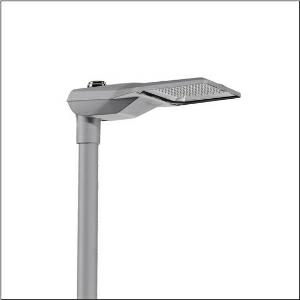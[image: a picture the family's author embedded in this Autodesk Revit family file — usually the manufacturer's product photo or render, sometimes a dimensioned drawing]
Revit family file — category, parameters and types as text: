
# Revit family: streetlight_sl_21_midi___p0_8a_5xe7u27n08lb_052f
name_source: partatom
category: Lighting Fixtures
units: mm (PartAtom-declared; Revit-internal decimal feet)

## family parameters
Cut with Voids When Loaded = No
Host = Face
Light Source = No
Part Type = Normal
Room Calculation Point = No
Round Connector Dimension = Use Diameter
Shared = No

## types (1)
- --- (1 x LED, 11980 lm, 98.3 W, 2200K)
    Apparent Load = 98 VA
    CIE Flux Codes = 33 69 96 100 100
    Color Rendering = 70
    Color Temperature = 2200K
    Default Elevation = 1800 mm
    Description = Streetlight SL 21 midi, mast luminaire, primary light control with lens, of PMMA, primary optical cover: cover, of toughened safety glass, transparent, light distribution: P0.8a, light emission: direct distribution, primary light characteristic: asymmetric, installation type: side-entry, LED, 3G 2.5mm², High Power LED, rated luminous flux: 11.980lm, luminous efficacy: 122lm/W, light colour: 722, colour temperature: 2200K, control gear: NEMA (7pin), control: flexible luminous flux parameterisation, time-dependent luminous flux control, constant luminous flux control, pre-setting: linear dimming characteristic, overheat protection, mains connection: 220..240V, AC, 50/60Hz, connection cable pre-assembled, cable length: 10,5m, wiring characteristics: H05VV-F, start of lifetime: 98W, end of service life: 101W, reduction: 45W, luminaire housing, of diecast aluminium (EN AC-44300), powder-coated, Siteco® metallic grey (DB 702S), corrosivity category C5 mid according to DIN EN ISO 12944, multi-level sealing system, sealing non-destructively replaceable, inclination adjustable: 0°, 5°, 10°, 15°, length: 644mm, width: 335mm, height: 110mm, spigot size: 42mm (side-entry), mounting height: 4..8m, protection rating (complete): IP66, insulation class (complete): insulation class I (protective earthing), certification: CE, ENEC, ENEC+, VDE, impact resistance: IK09, permissible operating ambient temperature for outdoor applications: -40..+50°C, standard-compliant lighting for roads and squares, packaging unit: 1 piece

Light Distribution: P0.8a
    Height = 111 mm
    Lamp = 1 x LED
    Lamp Light Flux = 11980 lm
    Lamp Power = 98.3 W
    Lamp count = 1
    Length = 644 mm
    Luminous efficacy = 122 lm/W
    Manufacturer = Siteco
    ModVariant = No
    Model = 5XE7U27N08LB
    Number of Poles = 1
    OnlyDefault = Yes
    Power Factor = 1
    Product Name = Streetlight SL 21 midi | P0.8a
    Product group = mast luminaire | pylon top
    ProductGroupID = 6100
    Protection Class = Protection class I
    Protection Degree = IP 66
    RLX_Detail_Level = 1
    RLX_Emergency_Light_Flux = 0 lm
    RLX_Emergency_Type = 0
    RLX_Emergency_Type_DB = No
    RlxData = <blob elided: 90061 chars, md5=1d34e739>
    Socket = socket
    Standby Power = 0 W
    System Light Flux = 11980 lm
    System Power = 98 W
    Type Comments = factory setting: luminous flux: 100 % | dim-lin: 254 | 1020 mA
    Type Image = l_1294377.jpg
    URL = http://relux.com
    VarID = @adj_070352
    Voltage = 0 V
    Weight = 0.00 kg
    Width = 336 mm

## geometry (parser evidence)
native form markers: Blend x4, Sweep x11
no freeform markers — native parametric forms only
